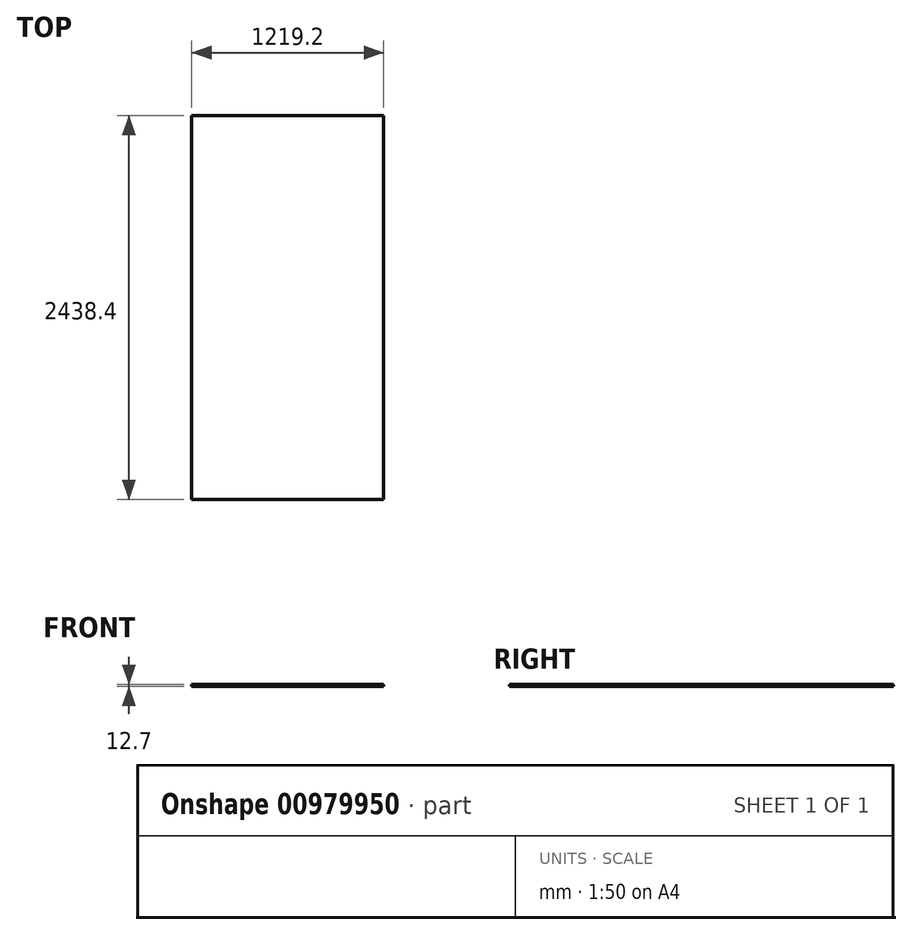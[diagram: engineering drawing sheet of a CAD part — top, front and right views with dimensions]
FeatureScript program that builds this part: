
annotation { "Feature Type Name" : "Feature", "Feature Type Description" : "" }
export const myFeature = defineFeature(function(context is Context, id is Id, definition is map)
    precondition{}
    {
        {
            var Q0;
            Q0=qCreatedBy(makeId("Top.planeOp"),FACE);
            var sketch = newSketch(context, id + "F0", { "sketchPlane" : qUnion([Q0])});
            skLineSegment(sketch, "E0.bottom", {"start": v(-609.6, 1219.2) * mm, "end": v(609.6, 1219.2) * mm});
            skLineSegment(sketch, "E0.top", {"start": v(-609.6, -1219.2) * mm, "end": v(609.6, -1219.2) * mm});
            skLineSegment(sketch, "E0.left", {"start": v(-609.6, 1219.2) * mm, "end": v(-609.6, -1219.2) * mm});
            skLineSegment(sketch, "E0.right", {"start": v(609.6, 1219.2) * mm, "end": v(609.6, -1219.2) * mm});
            skSolve(sketch);
        }
        {
            var Q0;
            Q0 = qSketchRegion(id + "F0", true);
            extrude(context, id + "F1", {"entities" : qUnion([Q0]), "oppositeDirection" : true, "depth" : 12.7 * mm, "offsetDistance" : 25.4 * mm});
        }
    });
